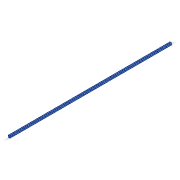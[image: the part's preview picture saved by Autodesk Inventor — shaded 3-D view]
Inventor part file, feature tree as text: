
AUTODESK INVENTOR PART (.ipt)
format: ipt  version: 2020 (Build 240168000, 168)  size: 170,496 bytes
history: mixed  units: in
note: dims shown in document units (in); Inventor stores cm internally (conversion verified against a paired STEP export)
features: direct_edit x1, fillet x1, other x1, imported_body x1
ambient origin geometry x8: Origin, YZ Plane, XZ Plane, XY Plane, X Axis, Y Axis, Z Axis, Center Point
bodies: Solid1 (imported_parasolid)
feature tree (4):
  direct_edit  "Direct Edit1"
  fillet  "Fillet1"  Radius=39.3701in
  other  "Size1"
  imported_body  NMx_Import_Brep_tag  [imported B-rep: ~63 faces, bbox_mm=[20.0, 20.0, 1500.0]]
